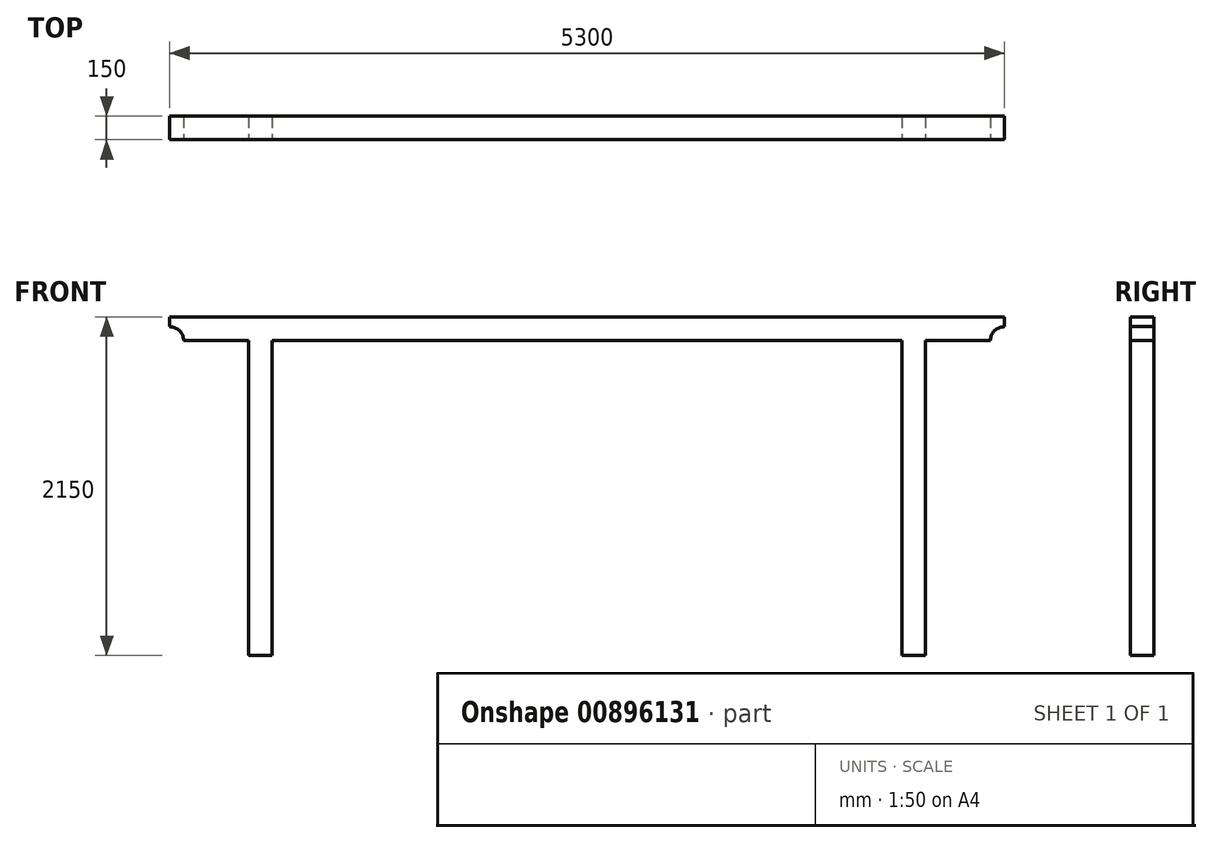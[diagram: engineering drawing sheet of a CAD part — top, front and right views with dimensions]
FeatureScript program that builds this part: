
annotation { "Feature Type Name" : "Feature", "Feature Type Description" : "" }
export const myFeature = defineFeature(function(context is Context, id is Id, definition is map)
    precondition{}
    {
        {
            var Q0;
            Q0=qCreatedBy(makeId("Front.planeOp"),FACE);
            var sketch = newSketch(context, id + "F0", { "sketchPlane" : qUnion([Q0])});
            skLineSegment(sketch, "E0.bottom", {"start": v(0, 0) * mm, "end": v(150, 0) * mm});
            skLineSegment(sketch, "E0.top", {"start": v(0, 2000) * mm, "end": v(150, 2000) * mm});
            skLineSegment(sketch, "E0.left", {"start": v(0, 0) * mm, "end": v(0, 2000) * mm});
            skLineSegment(sketch, "E0.right", {"start": v(150, 0) * mm, "end": v(150, 2000) * mm});
            skLineSegment(sketch, "E1.bottom", {"start": v(150, 2000) * mm, "end": v(650, 2000) * mm});
            skLineSegment(sketch, "E1.top", {"start": v(150, 2150) * mm, "end": v(650, 2150) * mm});
            skLineSegment(sketch, "E1.left", {"start": v(150, 2000) * mm, "end": v(150, 2150) * mm});
            skLineSegment(sketch, "E1.right", {"start": v(650, 2000) * mm, "end": v(650, 2150) * mm});
            skLineSegment(sketch, "E2.bottom", {"start": v(150, 2000) * mm, "end": v(-4150, 2000) * mm});
            skLineSegment(sketch, "E2.top", {"start": v(150, 2150) * mm, "end": v(-4150, 2150) * mm});
            skLineSegment(sketch, "E2.right", {"start": v(-4150, 2000) * mm, "end": v(-4150, 2150) * mm});
            skLineSegment(sketch, "E3.bottom", {"start": v(-4150, 2000) * mm, "end": v(-4000, 2000) * mm});
            skLineSegment(sketch, "E3.top", {"start": v(-4150, 0) * mm, "end": v(-4000, 0) * mm});
            skLineSegment(sketch, "E3.left", {"start": v(-4150, 2000) * mm, "end": v(-4150, 0) * mm});
            skLineSegment(sketch, "E3.right", {"start": v(-4000, 2000) * mm, "end": v(-4000, 0) * mm});
            skLineSegment(sketch, "E4.bottom", {"start": v(-4150, 2000) * mm, "end": v(-4650, 2000) * mm});
            skLineSegment(sketch, "E4.top", {"start": v(-4150, 2150) * mm, "end": v(-4650, 2150) * mm});
            skLineSegment(sketch, "E4.right", {"start": v(-4650, 2000) * mm, "end": v(-4650, 2150) * mm});
            skSolve(sketch);
        }
        {
            var Q0;
            Q0 = qSketchRegion(id + "F0", true);
            extrude(context, id + "F1", {"entities" : qUnion([Q0]), "oppositeDirection" : true, "depth" : 150 * mm, "offsetDistance" : 25 * mm});
        }
        {
            var Q0;
            Q0=sQuery(id+"F0.wireOp",VERTEX,"E4.bottom.end");
            var Q1;
            Q1=makeQuery(id+"F1.opExtrude","SWEPT_BODY",BODY,{"disambiguationData":[OSD([sQuery(id+"F0.wireOp",EDGE,"E0.bottom"),sQuery(id+"F0.wireOp",EDGE,"E0.left"),sQuery(id+"F0.wireOp",EDGE,"E0.right"),sQuery(id+"F0.wireOp",EDGE,"E1.bottom"),sQuery(id+"F0.wireOp",EDGE,"E1.top"),sQuery(id+"F0.wireOp",EDGE,"E1.right"),sQuery(id+"F0.wireOp",EDGE,"E2.bottom"),sQuery(id+"F0.wireOp",EDGE,"E2.top"),sQuery(id+"F0.wireOp",EDGE,"E3.top"),sQuery(id+"F0.wireOp",EDGE,"E3.left"),sQuery(id+"F0.wireOp",EDGE,"E3.right"),sQuery(id+"F0.wireOp",EDGE,"E4.bottom"),sQuery(id+"F0.wireOp",EDGE,"E4.top"),sQuery(id+"F0.wireOp",EDGE,"E4.right")])]});
            hole(context, id + "F2", {"style" : HoleStyle.SIMPLE, "endStyle" : HoleEndStyle.THROUGH, "holeDiameter" : 175 * mm, "majorDiameter" : 5 * mm, "isTappedThrough" : true, "tappedDepth" : 12 * mm, "tapClearance" : 3, "locations" : qUnion([Q0]), "scope" : qUnion([Q1])});
        }
        {
            var Q0;
            Q0=sQuery(id+"F0.wireOp",VERTEX,"E1.bottom.end");
            var Q1;
            Q1=makeQuery(id+"F1.opExtrude","SWEPT_BODY",BODY,{"disambiguationData":[OSD([sQuery(id+"F0.wireOp",EDGE,"E0.bottom"),sQuery(id+"F0.wireOp",EDGE,"E0.left"),sQuery(id+"F0.wireOp",EDGE,"E0.right"),sQuery(id+"F0.wireOp",EDGE,"E1.bottom"),sQuery(id+"F0.wireOp",EDGE,"E1.top"),sQuery(id+"F0.wireOp",EDGE,"E1.right"),sQuery(id+"F0.wireOp",EDGE,"E2.bottom"),sQuery(id+"F0.wireOp",EDGE,"E2.top"),sQuery(id+"F0.wireOp",EDGE,"E3.top"),sQuery(id+"F0.wireOp",EDGE,"E3.left"),sQuery(id+"F0.wireOp",EDGE,"E3.right"),sQuery(id+"F0.wireOp",EDGE,"E4.bottom"),sQuery(id+"F0.wireOp",EDGE,"E4.top"),sQuery(id+"F0.wireOp",EDGE,"E4.right")])]});
            hole(context, id + "F3", {"style" : HoleStyle.SIMPLE, "endStyle" : HoleEndStyle.THROUGH, "holeDiameter" : 175 * mm, "majorDiameter" : 5 * mm, "isTappedThrough" : true, "tappedDepth" : 12 * mm, "tapClearance" : 3, "locations" : qUnion([Q0]), "scope" : qUnion([Q1])});
        }
    });
